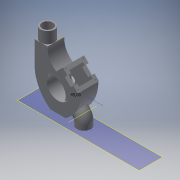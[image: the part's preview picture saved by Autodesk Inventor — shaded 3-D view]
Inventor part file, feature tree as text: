
AUTODESK INVENTOR PART (.ipt)
format: ipt  version: 2019 (Build 230136000, 136)  size: 378,880 bytes
history: native  units: mm
features: sketch x21, extrude x14, other x4, sweep x3, projected_geometry x3
ambient origin geometry x8: Origin, YZ Plane, XZ Plane, XY Plane, X Axis, Y Axis, Z Axis, Center Point
bodies: Body1 (feature_tree)
feature tree (45):
  extrude  "Extrusion2"  Depth=80.0mm
  sketch  "Esquisse3"
  sweep  "Balayage1"
  extrude  "Extrusion6"  Depth=30.0mm
  extrude  "Extrusion7"  Depth=18.0mm TaperAngle=0.0deg
  extrude  "Extrusion8"  TaperAngle=135.0deg  [1 undecoded]
  sketch  "Esquisse11"
  sketch  "Esquisse12"
  other  "Plan de construction1"
  sketch  "Esquisse13"
  extrude  "Extrusion9"  Depth=23.0mm
  extrude  "Extrusion10"  Depth=14.0mm
  other  "Plan de construction2"
  sketch  "Esquisse14"
  extrude  "Extrusion11"  Depth=4.0mm
  extrude  "Extrusion12"  TaperAngle=0.0deg  [1 undecoded]
  extrude  "Extrusion13"  Depth=4.0mm TaperAngle=0.0deg
  extrude  "Extrusion14"  Depth=9.0mm
  extrude  "Extrusion15"  Depth=4.0mm TaperAngle=0.0deg
  sketch  "Esquisse20"
  sketch  "Esquisse21"
  sketch  "Esquisse24"
  extrude  "Extrusion17"  Depth=2.0mm
  sweep  "Balayage4"
  extrude  "Extrusion18"  Depth=35.0mm
  sketch  "Esquisse28"
  other  "Plan de construction4"
  extrude  "Extrusion21"  Depth=17.5mm
  sketch  "Esquisse30"
  other  "Plan de construction5"
  sweep  "Balayage5"
  sketch  "Esquisse2"
  sketch  "Esquisse4"
  sketch  "Esquisse8"
  sketch  "Esquisse9"
  sketch  "Esquisse10"
  sketch  "Esquisse16"
  projected_geometry  "Boucle projetée3"
  sketch  "Esquisse18"
  sketch  "Esquisse19"
  projected_geometry  "Boucle projetée4"
  projected_geometry  "Boucle projetée6"
  sketch  "Esquisse25"
  sketch  "Esquisse29"
  sketch  "Esquisse31"
note: 2 required parameter values undecoded (feature->parameter linkage not recoverable at this tier; creation-order binding heuristic only, values carry confidence <= 0.55)
